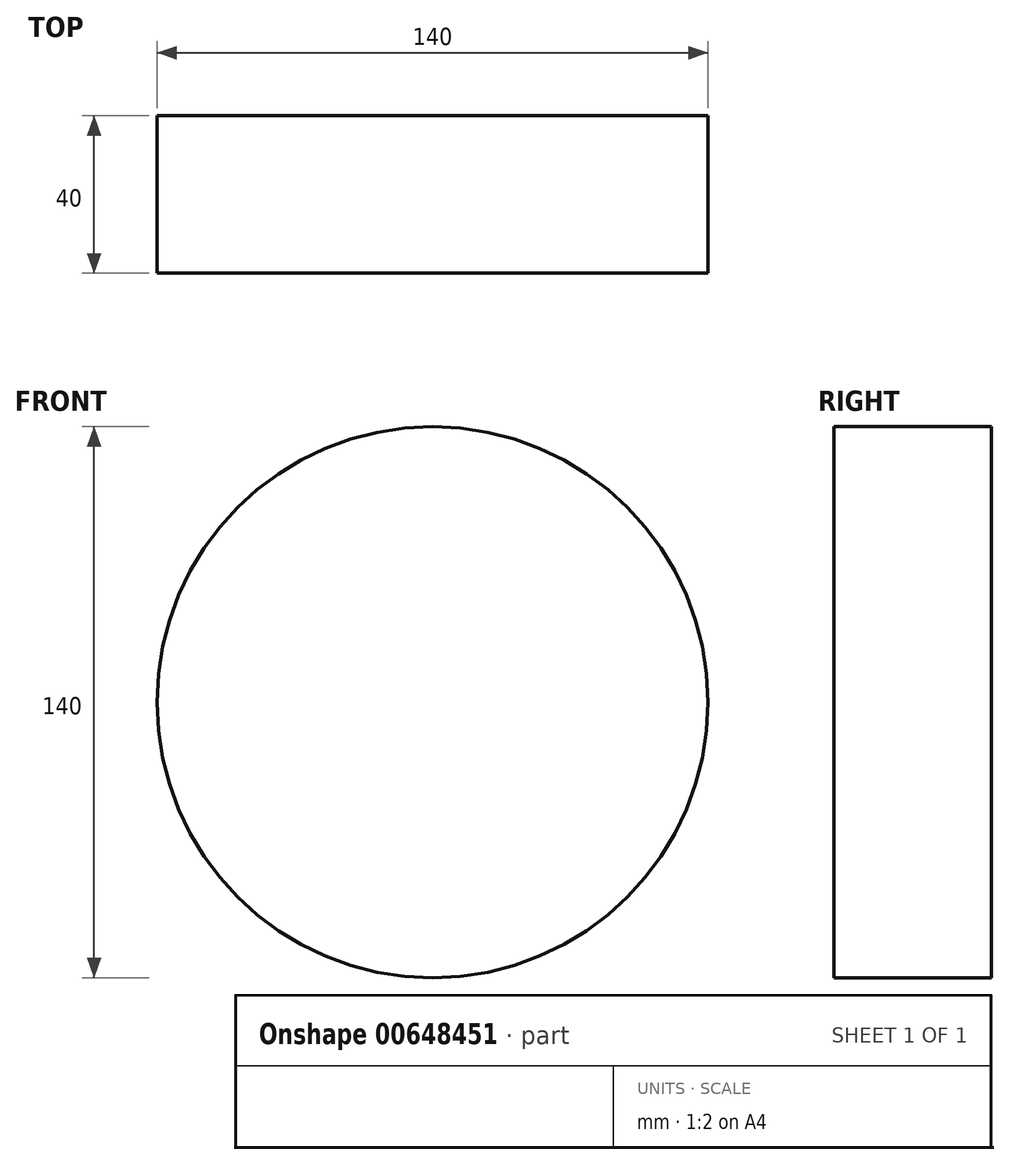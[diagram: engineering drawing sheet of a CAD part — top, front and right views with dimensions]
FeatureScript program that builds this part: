
annotation { "Feature Type Name" : "Feature", "Feature Type Description" : "" }
export const myFeature = defineFeature(function(context is Context, id is Id, definition is map)
    precondition{}
    {
        {
            var Q0;
            Q0=qCreatedBy(makeId("Front.planeOp"),FACE);
            var sketch = newSketch(context, id + "F0", { "sketchPlane" : qUnion([Q0])});
            skCircle(sketch, "E0", {"center": v(0, 0) * mm, "radius": 70 * mm});
            skSolve(sketch);
        }
        {
            var Q0;
            Q0=makeQuery(id+"F0.imprint","IMPRINT",FACE,{"disambiguationData":[TD([[makeQuery(id+"F0.imprint","IMPRINT",EDGE,{"derivedFrom":sQuery(id+"F0.wireOp",EDGE,"E0")}),1.0]])]});
            extrude(context, id + "F1", {"entities" : qUnion([Q0]), "depth" : 40 * mm, "offsetDistance" : 25 * mm});
        }
    });
